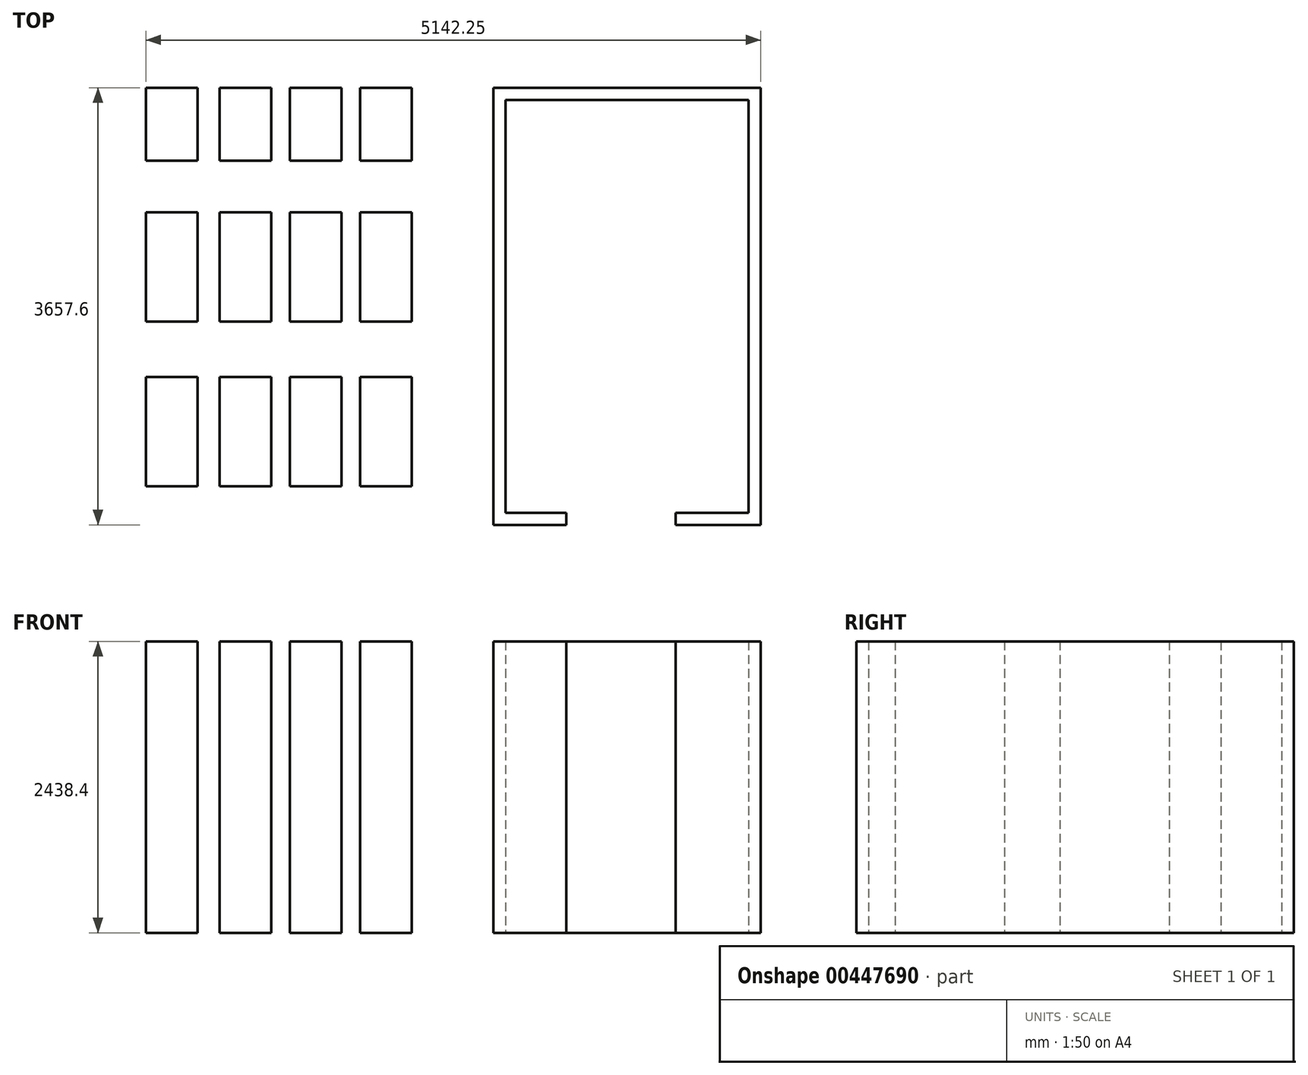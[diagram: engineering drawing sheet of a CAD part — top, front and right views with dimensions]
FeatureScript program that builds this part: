
annotation { "Feature Type Name" : "Feature", "Feature Type Description" : "" }
export const myFeature = defineFeature(function(context is Context, id is Id, definition is map)
    precondition{}
    {
        {
            var Q0;
            Q0=qCreatedBy(makeId("Top.planeOp"),FACE);
            var sketch = newSketch(context, id + "F0", { "sketchPlane" : qUnion([Q0])});
            skLineSegment(sketch, "E0", {"start": v(0, 0) * mm, "end": v(0, 3454.4) * mm});
            skLineSegment(sketch, "E1", {"start": v(0, 3454.4) * mm, "end": v(2032, 3454.4) * mm});
            skLineSegment(sketch, "E2", {"start": v(2032, 3454.4) * mm, "end": v(2032, 0) * mm});
            skLineSegment(sketch, "E3", {"start": v(2032, 0) * mm, "end": v(1422.4, 0) * mm});
            skLineSegment(sketch, "E4", {"start": v(0, 0) * mm, "end": v(508, 0) * mm});
            skLineSegment(sketch, "E5.0", {"start": v(2133.6, -101.6) * mm, "end": v(1422.4, -101.6) * mm});
            skLineSegment(sketch, "E5.1", {"start": v(-101.6, -101.6) * mm, "end": v(508, -101.6) * mm});
            skLineSegment(sketch, "E5.2", {"start": v(-101.6, -101.6) * mm, "end": v(-101.6, 3556) * mm});
            skLineSegment(sketch, "E5.3", {"start": v(-101.6, 3556) * mm, "end": v(2133.6, 3556) * mm});
            skLineSegment(sketch, "E5.4", {"start": v(2133.6, 3556) * mm, "end": v(2133.6, -101.6) * mm});
            skLineSegment(sketch, "E6", {"start": v(508, 0) * mm, "end": v(508, -101.6) * mm});
            skLineSegment(sketch, "E7", {"start": v(1422.4, -101.6) * mm, "end": v(1422.4, 0) * mm});
            skSolve(sketch);
        }
        {
            var Q0;
            Q0 = qSketchRegion(id + "F0", true);
            extrude(context, id + "F1", {"entities" : qUnion([Q0]), "depth" : 2438.4 * mm});
        }
        {
            var Q0;
            Q0=makeQuery(id+"F1.opExtrude","CAP_FACE",FACE,{"disambiguationData":[OSD([sQuery(id+"F0.wireOp",EDGE,"E0"),sQuery(id+"F0.wireOp",EDGE,"E1"),sQuery(id+"F0.wireOp",EDGE,"E2"),sQuery(id+"F0.wireOp",EDGE,"E3"),sQuery(id+"F0.wireOp",EDGE,"E4"),sQuery(id+"F0.wireOp",EDGE,"E5.0"),sQuery(id+"F0.wireOp",EDGE,"E5.1"),sQuery(id+"F0.wireOp",EDGE,"E5.2"),sQuery(id+"F0.wireOp",EDGE,"E5.3"),sQuery(id+"F0.wireOp",EDGE,"E5.4"),sQuery(id+"F0.wireOp",EDGE,"E6"),sQuery(id+"F0.wireOp",EDGE,"E7")])],"isStart":true});
            var sketch = newSketch(context, id + "F2", { "sketchPlane" : qUnion([Q0])});
            skLineSegment(sketch, "E8", {"start": v(-786.4, -3556) * mm, "end": v(-1218.2, -3556) * mm});
            skLineSegment(sketch, "E9", {"start": v(-1218.2, -3556) * mm, "end": v(-1218.2, -2946.4) * mm});
            skLineSegment(sketch, "E10", {"start": v(-1218.2, -2946.4) * mm, "end": v(-786.4, -2946.4) * mm});
            skLineSegment(sketch, "E11", {"start": v(-786.4, -2946.4) * mm, "end": v(-786.4, -3556) * mm});
            skLineSegment(sketch, "E12", {"start": v(-1218.2, -2512.56) * mm, "end": v(-786.4, -2512.56) * mm});
            skLineSegment(sketch, "E13", {"start": v(-786.4, -2512.56) * mm, "end": v(-786.4, -1598.16) * mm});
            skLineSegment(sketch, "E14", {"start": v(-786.4, -1598.16) * mm, "end": v(-1218.2, -1598.16) * mm});
            skLineSegment(sketch, "E15", {"start": v(-1218.2, -1598.16) * mm, "end": v(-1218.2, -2512.56) * mm});
            skLineSegment(sketch, "E16.MirrorCS", {"start": v(-786.4, -1135.48) * mm, "end": v(-1218.2, -1135.48) * mm});
            skLineSegment(sketch, "E17.MirrorCS", {"start": v(-1218.2, -1135.48) * mm, "end": v(-1218.2, -221.08) * mm});
            skLineSegment(sketch, "E18.MirrorCS", {"start": v(-1218.2, -221.08) * mm, "end": v(-786.4, -221.08) * mm});
            skLineSegment(sketch, "E19.MirrorCS", {"start": v(-786.4, -221.08) * mm, "end": v(-786.4, -1135.48) * mm});
            skLineSegment(sketch, "E20.MirrorCS", {"start": v(-2576.85, -2512.56) * mm, "end": v(-3008.65, -2512.56) * mm});
            skLineSegment(sketch, "E21.MirrorCS", {"start": v(-3008.65, -2512.56) * mm, "end": v(-3008.65, -1598.16) * mm});
            skLineSegment(sketch, "E22.MirrorCS", {"start": v(-3008.65, -1598.16) * mm, "end": v(-2576.85, -1598.16) * mm});
            skLineSegment(sketch, "E23.MirrorCS", {"start": v(-2576.85, -1598.16) * mm, "end": v(-2576.85, -2512.56) * mm});
            skLineSegment(sketch, "E24.MirrorCS", {"start": v(-3008.65, -221.08) * mm, "end": v(-3008.65, -1135.48) * mm});
            skLineSegment(sketch, "E25.MirrorCS", {"start": v(-3008.65, -1135.48) * mm, "end": v(-2576.85, -1135.48) * mm});
            skLineSegment(sketch, "E26.MirrorCS", {"start": v(-3008.65, -2946.4) * mm, "end": v(-3008.65, -3556) * mm});
            skLineSegment(sketch, "E27.MirrorCS", {"start": v(-3008.65, -3556) * mm, "end": v(-2576.85, -3556) * mm});
            skLineSegment(sketch, "E28.MirrorCS", {"start": v(-2576.85, -2946.4) * mm, "end": v(-3008.65, -2946.4) * mm});
            skLineSegment(sketch, "E29.MirrorCS", {"start": v(-2576.85, -1135.48) * mm, "end": v(-2576.85, -221.08) * mm});
            skLineSegment(sketch, "E30.MirrorCS", {"start": v(-2576.85, -221.08) * mm, "end": v(-3008.65, -221.08) * mm});
            skLineSegment(sketch, "E31.MirrorCS", {"start": v(-2576.85, -3556) * mm, "end": v(-2576.85, -2946.4) * mm});
            skLineSegment(sketch, "E32.1.0.0", {"start": v(-1373.13, -2512.56) * mm, "end": v(-1373.13, -1598.16) * mm});
            skLineSegment(sketch, "E32.1.0.1", {"start": v(-1804.93, -221.08) * mm, "end": v(-1373.13, -221.08) * mm});
            skLineSegment(sketch, "E32.1.0.2", {"start": v(-1804.93, -2512.56) * mm, "end": v(-1373.13, -2512.56) * mm});
            skLineSegment(sketch, "E32.1.0.3", {"start": v(-1804.93, -1135.48) * mm, "end": v(-1804.93, -221.08) * mm});
            skLineSegment(sketch, "E32.1.0.4", {"start": v(-1373.13, -3556) * mm, "end": v(-1804.93, -3556) * mm});
            skLineSegment(sketch, "E32.1.0.5", {"start": v(-1804.93, -3556) * mm, "end": v(-1804.93, -2946.4) * mm});
            skLineSegment(sketch, "E32.1.0.6", {"start": v(-1804.93, -2946.4) * mm, "end": v(-1373.13, -2946.4) * mm});
            skLineSegment(sketch, "E32.1.0.7", {"start": v(-1373.13, -2946.4) * mm, "end": v(-1373.13, -3556) * mm});
            skLineSegment(sketch, "E32.1.0.8", {"start": v(-1373.13, -221.08) * mm, "end": v(-1373.13, -1135.48) * mm});
            skLineSegment(sketch, "E32.1.0.9", {"start": v(-1373.13, -1598.16) * mm, "end": v(-1804.93, -1598.16) * mm});
            skLineSegment(sketch, "E32.1.0.10", {"start": v(-1804.93, -1598.16) * mm, "end": v(-1804.93, -2512.56) * mm});
            skLineSegment(sketch, "E32.1.0.11", {"start": v(-1373.13, -1135.48) * mm, "end": v(-1804.93, -1135.48) * mm});
            skLineSegment(sketch, "E32.2.0.0", {"start": v(-1959.87, -2512.56) * mm, "end": v(-1959.87, -1598.16) * mm});
            skLineSegment(sketch, "E32.2.0.1", {"start": v(-2391.67, -221.08) * mm, "end": v(-1959.87, -221.08) * mm});
            skLineSegment(sketch, "E32.2.0.2", {"start": v(-2391.67, -2512.56) * mm, "end": v(-1959.87, -2512.56) * mm});
            skLineSegment(sketch, "E32.2.0.3", {"start": v(-2391.67, -1135.48) * mm, "end": v(-2391.67, -221.08) * mm});
            skLineSegment(sketch, "E32.2.0.4", {"start": v(-1959.87, -3556) * mm, "end": v(-2391.67, -3556) * mm});
            skLineSegment(sketch, "E32.2.0.5", {"start": v(-2391.67, -3556) * mm, "end": v(-2391.67, -2946.4) * mm});
            skLineSegment(sketch, "E32.2.0.6", {"start": v(-2391.67, -2946.4) * mm, "end": v(-1959.87, -2946.4) * mm});
            skLineSegment(sketch, "E32.2.0.7", {"start": v(-1959.87, -2946.4) * mm, "end": v(-1959.87, -3556) * mm});
            skLineSegment(sketch, "E32.2.0.8", {"start": v(-1959.87, -221.08) * mm, "end": v(-1959.87, -1135.48) * mm});
            skLineSegment(sketch, "E32.2.0.9", {"start": v(-1959.87, -1598.16) * mm, "end": v(-2391.67, -1598.16) * mm});
            skLineSegment(sketch, "E32.2.0.10", {"start": v(-2391.67, -1598.16) * mm, "end": v(-2391.67, -2512.56) * mm});
            skLineSegment(sketch, "E32.2.0.11", {"start": v(-1959.87, -1135.48) * mm, "end": v(-2391.67, -1135.48) * mm});
            skLineSegment(sketch, "E32.direction1", {"start": v(-1218.2, -3556) * mm, "end": v(-1804.93, -3556) * mm, "construction": true});
            skSolve(sketch);
        }
        {
            var Q0;
            Q0 = qSketchRegion(id + "F2", true);
            extrude(context, id + "F3", {"entities" : qUnion([Q0]), "oppositeDirection" : true, "depth" : 2438.4 * mm});
        }
    });
